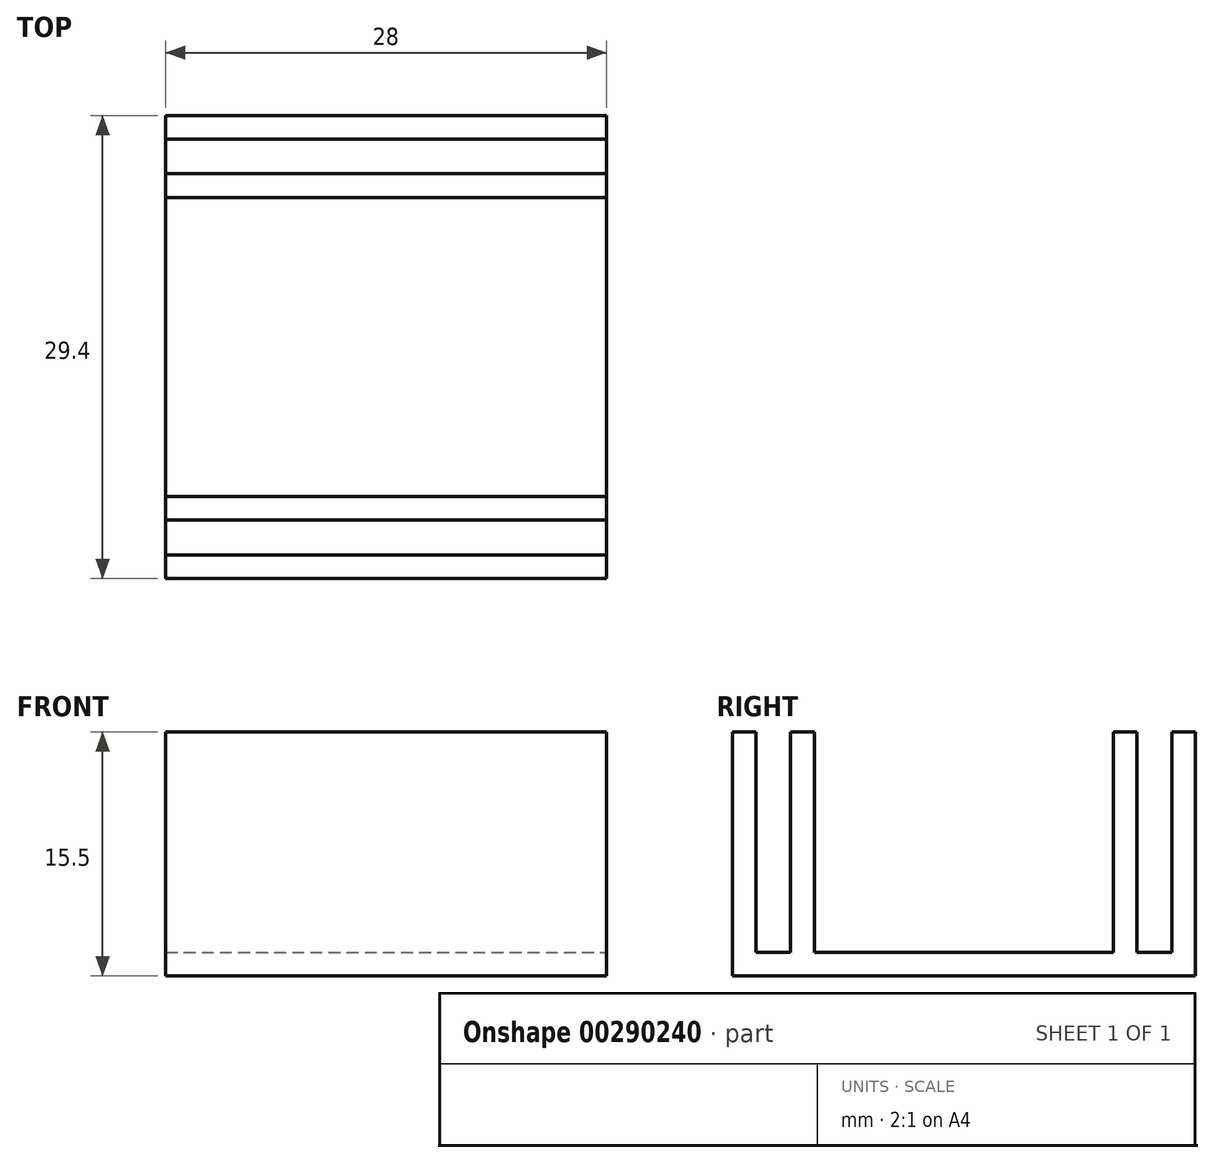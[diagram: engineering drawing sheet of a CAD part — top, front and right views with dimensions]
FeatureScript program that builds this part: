
annotation { "Feature Type Name" : "Feature", "Feature Type Description" : "" }
export const myFeature = defineFeature(function(context is Context, id is Id, definition is map)
    precondition{}
    {
        {
            var Q0;
            Q0=qCreatedBy(makeId("Top.planeOp"),FACE);
            var sketch = newSketch(context, id + "F0", { "sketchPlane" : qUnion([Q0])});
            skLineSegment(sketch, "E0.bottom", {"start": v(14, -14.7) * mm, "end": v(-14, -14.7) * mm});
            skLineSegment(sketch, "E0.top", {"start": v(14, 14.7) * mm, "end": v(-14, 14.7) * mm});
            skLineSegment(sketch, "E0.left", {"start": v(14, -14.7) * mm, "end": v(14, 14.7) * mm});
            skLineSegment(sketch, "E0.right", {"start": v(-14, -14.7) * mm, "end": v(-14, 14.7) * mm});
            skPoint(sketch, "E0.middle", {"position": v(0, 0) * mm});
            skSolve(sketch);
        }
        {
            var Q0;
            Q0 = qSketchRegion(id + "F0", true);
            extrude(context, id + "F1", {"entities" : qUnion([Q0]), "depth" : 1.5 * mm});
        }
        {
            var Q0;
            Q0=makeQuery(id+"F1.opExtrude","CAP_FACE",FACE,{"disambiguationData":[OSD([sQuery(id+"F0.wireOp",EDGE,"E0.bottom"),sQuery(id+"F0.wireOp",EDGE,"E0.top"),sQuery(id+"F0.wireOp",EDGE,"E0.left"),sQuery(id+"F0.wireOp",EDGE,"E0.right")])],"isStart":false});
            var sketch = newSketch(context, id + "F2", { "sketchPlane" : qUnion([Q0])});
            skLineSegment(sketch, "E1.bottom", {"start": v(-14, 9.5) * mm, "end": v(14, 9.5) * mm});
            skLineSegment(sketch, "E1.top", {"start": v(-14, 11) * mm, "end": v(14, 11) * mm});
            skLineSegment(sketch, "E1.left", {"start": v(-14, 9.5) * mm, "end": v(-14, 11) * mm});
            skLineSegment(sketch, "E1.right", {"start": v(14, 9.5) * mm, "end": v(14, 11) * mm});
            skLineSegment(sketch, "E2.bottom", {"start": v(-14, -11) * mm, "end": v(14, -11) * mm});
            skLineSegment(sketch, "E2.top", {"start": v(-14, -9.5) * mm, "end": v(14, -9.5) * mm});
            skLineSegment(sketch, "E2.left", {"start": v(-14, -11) * mm, "end": v(-14, -9.5) * mm});
            skLineSegment(sketch, "E2.right", {"start": v(14, -11) * mm, "end": v(14, -9.5) * mm});
            skLineSegment(sketch, "E3.bottom", {"start": v(-14, 13.2) * mm, "end": v(14, 13.2) * mm});
            skLineSegment(sketch, "E3.top", {"start": v(-14, 14.7) * mm, "end": v(14, 14.7) * mm});
            skLineSegment(sketch, "E3.left", {"start": v(-14, 13.2) * mm, "end": v(-14, 14.7) * mm});
            skLineSegment(sketch, "E3.right", {"start": v(14, 13.2) * mm, "end": v(14, 14.7) * mm});
            skLineSegment(sketch, "E4.bottom", {"start": v(-14, -14.7) * mm, "end": v(14, -14.7) * mm});
            skLineSegment(sketch, "E4.top", {"start": v(-14, -13.2) * mm, "end": v(14, -13.2) * mm});
            skLineSegment(sketch, "E4.left", {"start": v(-14, -14.7) * mm, "end": v(-14, -13.2) * mm});
            skLineSegment(sketch, "E4.right", {"start": v(14, -14.7) * mm, "end": v(14, -13.2) * mm});
            skSolve(sketch);
        }
        {
            var Q0;
            Q0 = qSketchRegion(id + "F2", true);
            extrude(context, id + "F3", {"entities" : qUnion([Q0]), "operationType" : NewBodyOperationType.ADD, "depth" : 14 * mm});
        }
    });
